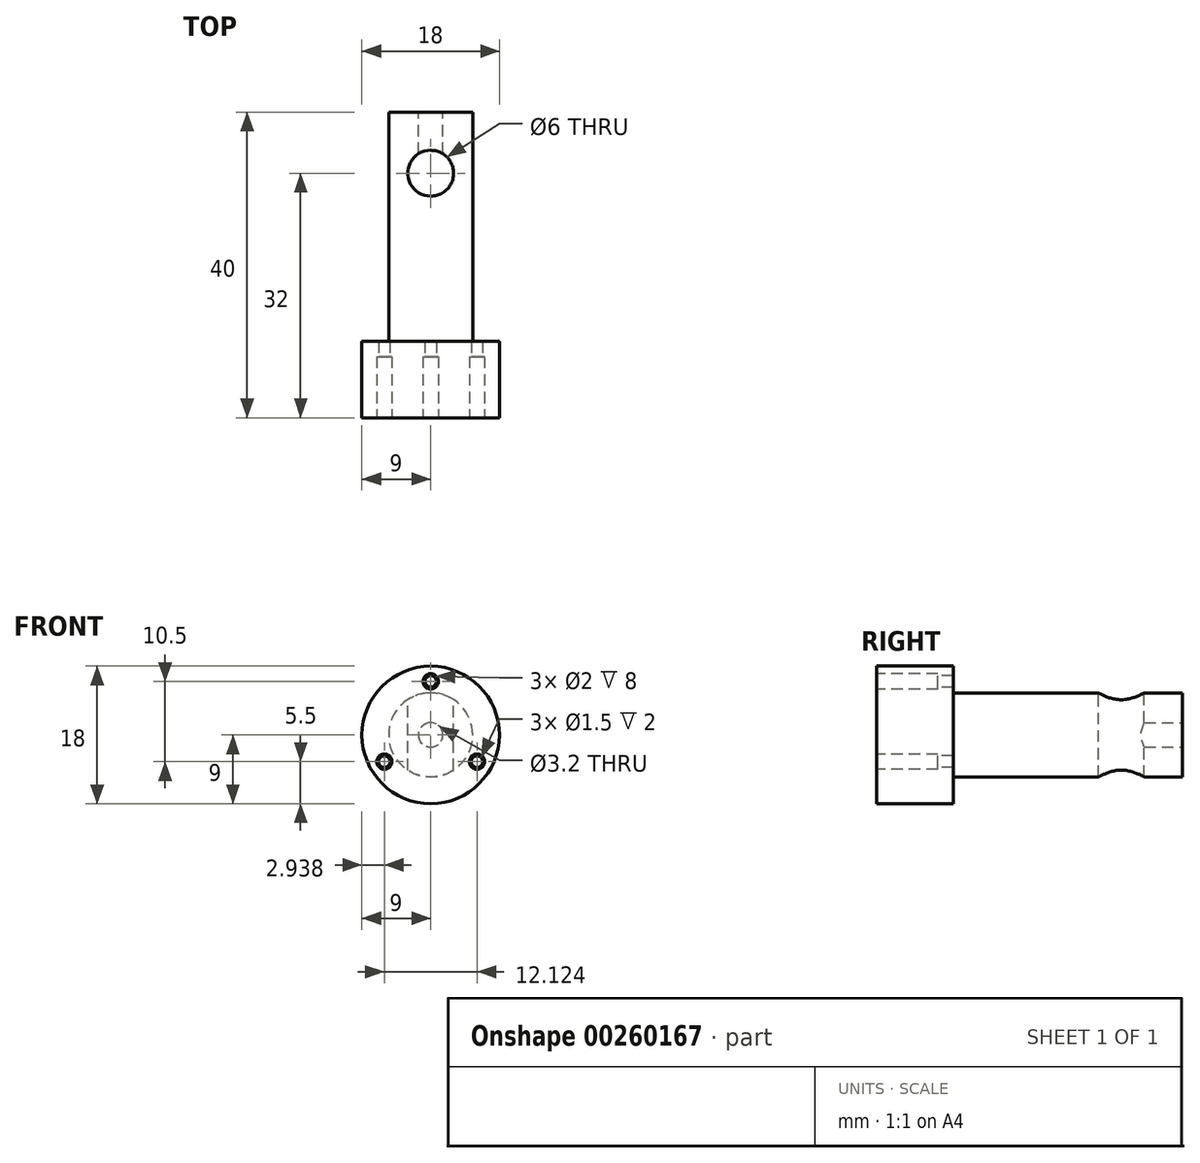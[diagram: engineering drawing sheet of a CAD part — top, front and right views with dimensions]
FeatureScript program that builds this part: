
annotation { "Feature Type Name" : "Feature", "Feature Type Description" : "" }
export const myFeature = defineFeature(function(context is Context, id is Id, definition is map)
    precondition{}
    {
        {
            var Q0;
            Q0=qCreatedBy(makeId("Front.planeOp"),FACE);
            var sketch = newSketch(context, id + "F0", { "sketchPlane" : qUnion([Q0])});
            skCircle(sketch, "E0", {"center": v(0, 0) * mm, "radius": 9 * mm});
            skSolve(sketch);
        }
        {
            var Q0;
            Q0=makeQuery(id+"F0.imprint","IMPRINT",FACE,{"disambiguationData":[TD([[makeQuery(id+"F0.imprint","IMPRINT",EDGE,{"derivedFrom":sQuery(id+"F0.wireOp",EDGE,"E0")}),1.0]])]});
            extrude(context, id + "F1", {"entities" : qUnion([Q0]), "endBound" : BoundingType.SYMMETRIC, "depth" : 40 * mm});
        }
        {
            var Q0;
            Q0=makeQuery(id+"F1.opExtrude","CAP_FACE",FACE,{"disambiguationData":[OSD([sQuery(id+"F0.wireOp",EDGE,"E0")])],"isStart":false});
            var sketch = newSketch(context, id + "F2", { "sketchPlane" : qUnion([Q0])});
            skArc(sketch, "E1", {"start": v(-1, 6.93) * mm, "mid": v(-6.06, 3.5) * mm, "end": v(-6.5, -2.6) * mm});
            skCircle(sketch, "E2", {"center": v(0, 7) * mm, "radius": 1 * mm});
            skCircle(sketch, "E3.1.0", {"center": v(-6.06, -3.5) * mm, "radius": 1 * mm});
            skCircle(sketch, "E3.2.0", {"center": v(6.06, -3.5) * mm, "radius": 1 * mm});
            skArc(sketch, "E4.trimOffspring", {"start": v(-5.5, -4.33) * mm, "mid": v(0, -7) * mm, "end": v(5.5, -4.33) * mm});
            skArc(sketch, "E5.trimOffspring", {"start": v(6.5, -2.6) * mm, "mid": v(6.06, 3.5) * mm, "end": v(1, 6.93) * mm});
            skCircle(sketch, "E6", {"center": v(-4, 0) * mm, "radius": 1.5 * mm});
            skCircle(sketch, "E7.MirrorC", {"center": v(4, 0) * mm, "radius": 1.5 * mm});
            skCircle(sketch, "E8", {"center": v(-6.06, -3.5) * mm, "radius": 0.75 * mm});
            skCircle(sketch, "E9.1.0", {"center": v(6.06, -3.5) * mm, "radius": 0.75 * mm});
            skCircle(sketch, "E9.2.0", {"center": v(0, 7) * mm, "radius": 0.75 * mm});
            skSolve(sketch);
        }
        {
            var Q0;
            {var subQ0=sQuery(id+"F2.wireOp",EDGE,"E2");var subQ1=makeQuery(id+"F2.imprint","INTERSECT",VERTEX,{"derivedFrom":[sQuery(id+"F2.wireOp",EDGE,"E1"),subQ0]});Q0=makeQuery(id+"F2.imprint","IMPRINT",FACE,{"disambiguationData":[TD([[makeQuery(id+"F2.imprint","IMPRINT",EDGE,{"disambiguationData":[TD([[subQ1,-1.0]])],"derivedFrom":subQ0}),1.0]])]});}
            var Q1;
            {var subQ0=sQuery(id+"F2.wireOp",EDGE,"E3.1.0");var subQ1=makeQuery(id+"F2.imprint","INTERSECT",VERTEX,{"derivedFrom":[sQuery(id+"F2.wireOp",EDGE,"E1"),subQ0]});Q1=makeQuery(id+"F2.imprint","IMPRINT",FACE,{"disambiguationData":[TD([[makeQuery(id+"F2.imprint","IMPRINT",EDGE,{"disambiguationData":[TD([[subQ1,1.0]])],"derivedFrom":subQ0}),1.0]])]});}
            var Q2;
            {var subQ0=sQuery(id+"F2.wireOp",EDGE,"E3.2.0");var subQ1=makeQuery(id+"F2.imprint","INTERSECT",VERTEX,{"derivedFrom":[subQ0,sQuery(id+"F2.wireOp",EDGE,"E4.trimOffspring")]});Q2=makeQuery(id+"F2.imprint","IMPRINT",FACE,{"disambiguationData":[TD([[makeQuery(id+"F2.imprint","IMPRINT",EDGE,{"disambiguationData":[TD([[subQ1,1.0]])],"derivedFrom":subQ0}),1.0]])]});}
            extrude(context, id + "F3", {"entities" : qUnion([Q0, Q1, Q2]), "operationType" : NewBodyOperationType.REMOVE, "oppositeDirection" : true, "depth" : 8 * mm});
        }
        {
            var Q0;
            Q0=makeQuery(id+"F1.opExtrude","CAP_FACE",FACE,{"disambiguationData":[OSD([sQuery(id+"F0.wireOp",EDGE,"E0")])],"isStart":true});
            var sketch = newSketch(context, id + "F4", { "sketchPlane" : qUnion([Q0])});
            skCircle(sketch, "E10", {"center": v(0, 0) * mm, "radius": 5.5 * mm});
            skSolve(sketch);
        }
        {
            var Q0;
            Q0=makeQuery(id+"F4.imprint","IMPRINT",FACE,{"disambiguationData":[TD([[makeQuery(id+"F4.imprint","IMPRINT",EDGE,{"derivedFrom":sQuery(id+"F4.wireOp",EDGE,"E10")}),-1.0]])]});
            extrude(context, id + "F5", {"entities" : qUnion([Q0]), "operationType" : NewBodyOperationType.REMOVE, "oppositeDirection" : true, "depth" : 30 * mm});
        }
        {
            var Q0;
            Q0=makeQuery(id+"F2.imprint","IMPRINT",FACE,{"disambiguationData":[TD([[makeQuery(id+"F2.imprint","IMPRINT",EDGE,{"derivedFrom":sQuery(id+"F2.wireOp",EDGE,"E8")}),1.0]])]});
            var Q1;
            Q1=makeQuery(id+"F2.imprint","IMPRINT",FACE,{"disambiguationData":[TD([[makeQuery(id+"F2.imprint","IMPRINT",EDGE,{"derivedFrom":sQuery(id+"F2.wireOp",EDGE,"E9.2.0")}),1.0]])]});
            var Q2;
            Q2=makeQuery(id+"F2.imprint","IMPRINT",FACE,{"disambiguationData":[TD([[makeQuery(id+"F2.imprint","IMPRINT",EDGE,{"derivedFrom":sQuery(id+"F2.wireOp",EDGE,"E9.1.0")}),1.0]])]});
            extrude(context, id + "F6", {"entities" : qUnion([Q0, Q1, Q2]), "operationType" : NewBodyOperationType.REMOVE, "oppositeDirection" : true, "depth" : 10 * mm});
        }
        {
            var Q0;
            Q0=qCreatedBy(makeId("Top.planeOp"),FACE);
            var sketch = newSketch(context, id + "F7", { "sketchPlane" : qUnion([Q0])});
            skCircle(sketch, "E11", {"center": v(0, 12) * mm, "radius": 3 * mm});
            skSolve(sketch);
        }
        {
            var Q0;
            Q0 = qSketchRegion(id + "F7", true);
            extrude(context, id + "F8", {"entities" : qUnion([Q0]), "operationType" : NewBodyOperationType.REMOVE, "endBound" : BoundingType.SYMMETRIC, "oppositeDirection" : true, "depth" : 25 * mm});
        }
        {
            var Q0;
            Q0=makeQuery(id+"F1.opExtrude","CAP_FACE",FACE,{"disambiguationData":[OSD([sQuery(id+"F0.wireOp",EDGE,"E0")])],"isStart":true});
            var sketch = newSketch(context, id + "F9", { "sketchPlane" : qUnion([Q0])});
            skPoint(sketch, "E12", {"position": v(0, 0) * mm});
            skSolve(sketch);
        }
        {
            var Q0;
            Q0=sQuery(id+"F9.wireOp",VERTEX,"E12");
            var Q1;
            Q1=makeQuery(id+"F1.opExtrude","SWEPT_BODY",BODY,{"disambiguationData":[OSD([sQuery(id+"F0.wireOp",EDGE,"E0")])]});
            hole(context, id + "F10", {"style" : HoleStyle.SIMPLE, "endStyle" : HoleEndStyle.BLIND, "standardTappedOrClearance" : lookupTablePath({ "standard" : "ISO", "engagement" : "75%", "pitch" : "0.75 mm", "size" : "M4", "type" : "Tapped" }), "standardBlindInLast" : lookupTablePath({ "standard" : "ISO", "engagement" : "75%", "pitch" : "0.75 mm", "size" : "M4", "type" : "Tapped" }), "holeDiameter" : 3.2 * mm, "showTappedDepth" : true, "holeDepth" : 7.25 * mm, "isTappedThrough" : true, "tappedDepth" : 5 * mm, "tapClearance" : 3, "startFromSketch" : true, "locations" : qUnion([Q0]), "scope" : qUnion([Q1])});
        }
    });
